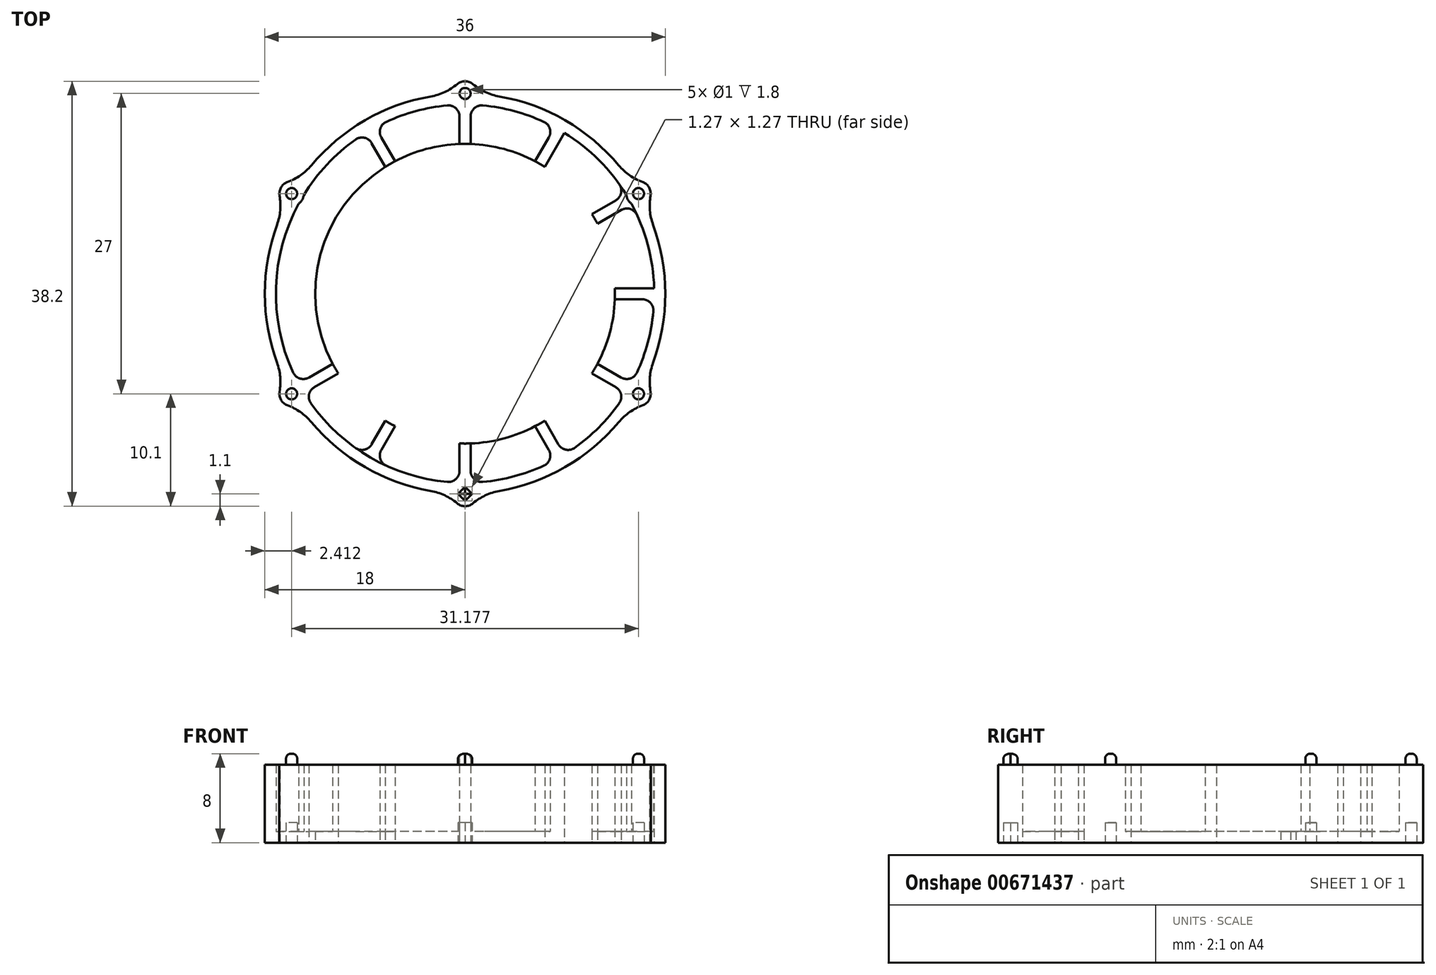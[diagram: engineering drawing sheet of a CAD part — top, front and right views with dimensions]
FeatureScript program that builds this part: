
annotation { "Feature Type Name" : "Feature", "Feature Type Description" : "" }
export const myFeature = defineFeature(function(context is Context, id is Id, definition is map)
    precondition{}
    {
        {
            var Q0;
            Q0=qCreatedBy(makeId("Top.planeOp"),FACE);
            var sketch = newSketch(context, id + "F0", { "sketchPlane" : qUnion([Q0])});
            skCircle(sketch, "E0", {"center": v(0, 0) * mm, "radius": 18 * mm});
            skCircle(sketch, "E1.0", {"center": v(0, 0) * mm, "radius": 17 * mm});
            skLineSegment(sketch, "E2.bottom", {"start": v(8.56, 15.83) * mm, "end": v(9.43, 15.33) * mm});
            skLineSegment(sketch, "E2.top", {"start": v(-9.43, -15.33) * mm, "end": v(-8.56, -15.83) * mm});
            skLineSegment(sketch, "E2.left", {"start": v(8.56, 15.83) * mm, "end": v(-9.43, -15.33) * mm});
            skLineSegment(sketch, "E2.right", {"start": v(9.43, 15.33) * mm, "end": v(-8.56, -15.83) * mm});
            skLineSegment(sketch, "E3.bottom", {"start": v(15.33, 9.43) * mm, "end": v(15.83, 8.56) * mm});
            skLineSegment(sketch, "E3.top", {"start": v(-15.83, -8.56) * mm, "end": v(-15.33, -9.43) * mm});
            skLineSegment(sketch, "E3.left", {"start": v(15.33, 9.43) * mm, "end": v(-15.83, -8.56) * mm});
            skLineSegment(sketch, "E3.right", {"start": v(15.83, 8.56) * mm, "end": v(-15.33, -9.43) * mm});
            skLineSegment(sketch, "E4", {"start": v(-38.35, 0) * mm, "end": v(39.17, 0) * mm, "construction": true});
            skLineSegment(sketch, "E5", {"start": v(0, 42.5) * mm, "end": v(0, -42.47) * mm, "construction": true});
            skLineSegment(sketch, "E6.bottom", {"start": v(-18, 0.5) * mm, "end": v(18, 0.5) * mm});
            skLineSegment(sketch, "E6.top", {"start": v(-18, -0.5) * mm, "end": v(18, -0.5) * mm});
            skLineSegment(sketch, "E6.left", {"start": v(-18, 0.5) * mm, "end": v(-18, -0.5) * mm});
            skLineSegment(sketch, "E6.right", {"start": v(18, 0.5) * mm, "end": v(18, -0.5) * mm});
            skLineSegment(sketch, "E7.bottom", {"start": v(-15.33, 9.43) * mm, "end": v(15.83, -8.56) * mm});
            skLineSegment(sketch, "E7.top", {"start": v(-15.83, 8.56) * mm, "end": v(15.33, -9.43) * mm});
            skLineSegment(sketch, "E7.left", {"start": v(-15.33, 9.43) * mm, "end": v(-15.83, 8.56) * mm});
            skLineSegment(sketch, "E7.right", {"start": v(15.83, -8.56) * mm, "end": v(15.33, -9.43) * mm});
            skLineSegment(sketch, "E8.bottom", {"start": v(-0.5, 18) * mm, "end": v(0.5, 18) * mm});
            skLineSegment(sketch, "E8.top", {"start": v(-0.5, -18) * mm, "end": v(0.5, -18) * mm});
            skLineSegment(sketch, "E8.left", {"start": v(-0.5, 18) * mm, "end": v(-0.5, -18) * mm});
            skLineSegment(sketch, "E8.right", {"start": v(0.5, 18) * mm, "end": v(0.5, -18) * mm});
            skLineSegment(sketch, "E9.bottom", {"start": v(-9.43, 15.33) * mm, "end": v(-8.56, 15.83) * mm});
            skLineSegment(sketch, "E9.top", {"start": v(8.56, -15.83) * mm, "end": v(9.43, -15.33) * mm});
            skLineSegment(sketch, "E9.left", {"start": v(-9.43, 15.33) * mm, "end": v(8.56, -15.83) * mm});
            skLineSegment(sketch, "E9.right", {"start": v(-8.56, 15.83) * mm, "end": v(9.43, -15.33) * mm});
            skCircle(sketch, "E10", {"center": v(0, 0) * mm, "radius": 13.47 * mm});
            skSolve(sketch);
        }
        {
            var Q0;
            Q0=qCreatedBy(makeId("Top.planeOp"),FACE);
            var sketch = newSketch(context, id + "F1", { "sketchPlane" : qUnion([Q0])});
            skCircle(sketch, "E11", {"center": v(0, 0) * mm, "radius": 18 * mm});
            skCircle(sketch, "E12", {"center": v(0, 0) * mm, "radius": 17 * mm});
            skSolve(sketch);
        }
        {
            var Q0;
            Q0=makeQuery(id+"F1.imprint","IMPRINT",FACE,{"disambiguationData":[TD([[makeQuery(id+"F1.imprint","IMPRINT",EDGE,{"derivedFrom":sQuery(id+"F1.wireOp",EDGE,"E11")}),1.0]])]});
            extrude(context, id + "F2", {"entities" : qUnion([Q0]), "depth" : 7 * mm, "offsetDistance" : 25 * mm});
        }
        {
            var Q0;
            {var subQ0=sQuery(id+"F0.wireOp",EDGE,"E2.right");var subQ1=sQuery(id+"F0.wireOp",EDGE,"E1.0");var subQ2=makeQuery(id+"F0.imprint","INTERSECT",VERTEX,{"disambiguationData":[OD(0.0)],"derivedFrom":[subQ1,subQ0]});Q0=makeQuery(id+"F0.imprint","IMPRINT",FACE,{"disambiguationData":[TD([[makeQuery(id+"F0.imprint","IMPRINT",EDGE,{"disambiguationData":[TD([[subQ2,-1.0]])],"derivedFrom":subQ1}),1.0]])]});}
            var Q1;
            {var subQ0=sQuery(id+"F0.wireOp",EDGE,"E6.bottom");var subQ1=sQuery(id+"F0.wireOp",EDGE,"E1.0");var subQ2=makeQuery(id+"F0.imprint","INTERSECT",VERTEX,{"disambiguationData":[OD(0.0)],"derivedFrom":[subQ1,subQ0]});Q1=makeQuery(id+"F0.imprint","IMPRINT",FACE,{"disambiguationData":[TD([[makeQuery(id+"F0.imprint","IMPRINT",EDGE,{"disambiguationData":[TD([[subQ2,1.0]])],"derivedFrom":subQ1}),1.0]])]});}
            var Q2;
            {var subQ0=sQuery(id+"F0.wireOp",EDGE,"E8.left");var subQ1=sQuery(id+"F0.wireOp",EDGE,"E1.0");var subQ2=makeQuery(id+"F0.imprint","INTERSECT",VERTEX,{"disambiguationData":[OD(1.0)],"derivedFrom":[subQ1,subQ0]});Q2=makeQuery(id+"F0.imprint","IMPRINT",FACE,{"disambiguationData":[TD([[makeQuery(id+"F0.imprint","IMPRINT",EDGE,{"disambiguationData":[TD([[subQ2,-1.0]])],"derivedFrom":subQ1}),1.0]])]});}
            var Q3;
            {var subQ0=sQuery(id+"F0.wireOp",EDGE,"E3.left");var subQ1=sQuery(id+"F0.wireOp",EDGE,"E1.0");var subQ2=makeQuery(id+"F0.imprint","INTERSECT",VERTEX,{"disambiguationData":[OD(1.0)],"derivedFrom":[subQ1,subQ0]});Q3=makeQuery(id+"F0.imprint","IMPRINT",FACE,{"disambiguationData":[TD([[makeQuery(id+"F0.imprint","IMPRINT",EDGE,{"disambiguationData":[TD([[subQ2,-1.0]])],"derivedFrom":subQ1}),1.0]])]});}
            var Q4;
            {var subQ0=sQuery(id+"F0.wireOp",EDGE,"E9.right");var subQ1=sQuery(id+"F0.wireOp",EDGE,"E1.0");var subQ2=makeQuery(id+"F0.imprint","INTERSECT",VERTEX,{"disambiguationData":[OD(0.0)],"derivedFrom":[subQ1,subQ0]});Q4=makeQuery(id+"F0.imprint","IMPRINT",FACE,{"disambiguationData":[TD([[makeQuery(id+"F0.imprint","IMPRINT",EDGE,{"disambiguationData":[TD([[subQ2,-1.0]])],"derivedFrom":subQ1}),1.0]])]});}
            var Q5;
            {var subQ0=sQuery(id+"F0.wireOp",EDGE,"E8.right");var subQ1=sQuery(id+"F0.wireOp",EDGE,"E1.0");var subQ2=makeQuery(id+"F0.imprint","INTERSECT",VERTEX,{"disambiguationData":[OD(0.0)],"derivedFrom":[subQ1,subQ0]});Q5=makeQuery(id+"F0.imprint","IMPRINT",FACE,{"disambiguationData":[TD([[makeQuery(id+"F0.imprint","IMPRINT",EDGE,{"disambiguationData":[TD([[subQ2,-1.0]])],"derivedFrom":subQ1}),1.0]])]});}
            var Q6;
            {var subQ0=sQuery(id+"F0.wireOp",EDGE,"E7.top");var subQ1=sQuery(id+"F0.wireOp",EDGE,"E1.0");var subQ2=makeQuery(id+"F0.imprint","INTERSECT",VERTEX,{"disambiguationData":[OD(1.0)],"derivedFrom":[subQ1,subQ0]});Q6=makeQuery(id+"F0.imprint","IMPRINT",FACE,{"disambiguationData":[TD([[makeQuery(id+"F0.imprint","IMPRINT",EDGE,{"disambiguationData":[TD([[subQ2,-1.0]])],"derivedFrom":subQ1}),1.0]])]});}
            var Q7;
            {var subQ0=sQuery(id+"F0.wireOp",EDGE,"E9.left");var subQ1=sQuery(id+"F0.wireOp",EDGE,"E1.0");var subQ2=makeQuery(id+"F0.imprint","INTERSECT",VERTEX,{"disambiguationData":[OD(1.0)],"derivedFrom":[subQ1,subQ0]});Q7=makeQuery(id+"F0.imprint","IMPRINT",FACE,{"disambiguationData":[TD([[makeQuery(id+"F0.imprint","IMPRINT",EDGE,{"disambiguationData":[TD([[subQ2,-1.0]])],"derivedFrom":subQ1}),1.0]])]});}
            extrude(context, id + "F3", {"entities" : qUnion([Q0, Q1, Q2, Q3, Q4, Q5, Q6, Q7]), "operationType" : NewBodyOperationType.ADD, "depth" : 7 * mm, "offsetDistance" : 25 * mm});
        }
        {
            var Q0;
            Q0=makeQuery(id+"F1.imprint","IMPRINT",FACE,{"disambiguationData":[TD([[makeQuery(id+"F1.imprint","IMPRINT",EDGE,{"derivedFrom":sQuery(id+"F1.wireOp",EDGE,"E11")}),1.0]])]});
            var Q1;
            Q1=makeQuery(id+"F1.imprint","IMPRINT",FACE,{"disambiguationData":[TD([[makeQuery(id+"F1.imprint","IMPRINT",EDGE,{"derivedFrom":sQuery(id+"F1.wireOp",EDGE,"E12")}),1.0]])]});
            extrude(context, id + "F4", {"entities" : qUnion([Q0, Q1]), "operationType" : NewBodyOperationType.ADD, "depth" : 1 * mm, "offsetDistance" : 25 * mm});
        }
        {
            var Q0;
            Q0=qCreatedBy(makeId("Top.planeOp"),FACE);
            var sketch = newSketch(context, id + "F5", { "sketchPlane" : qUnion([Q0])});
            skCircle(sketch, "E13", {"center": v(0, 0) * mm, "radius": 18 * mm});
            skLineSegment(sketch, "E14", {"start": v(0, 18) * mm, "end": v(0, -18) * mm, "construction": true});
            skLineSegment(sketch, "E15", {"start": v(15.59, 9) * mm, "end": v(0, 0) * mm, "construction": true});
            skLineSegment(sketch, "E16", {"start": v(9, 15.59) * mm, "end": v(0, 0) * mm, "construction": true});
            skLineSegment(sketch, "E17", {"start": v(0, 0) * mm, "end": v(18, 0) * mm, "construction": true});
            skLineSegment(sketch, "E18", {"start": v(0, 0) * mm, "end": v(15.59, -9) * mm, "construction": true});
            skLineSegment(sketch, "E19", {"start": v(0, 0) * mm, "end": v(9, -15.59) * mm, "construction": true});
            skLineSegment(sketch, "E20", {"start": v(0, 0) * mm, "end": v(-9, 15.59) * mm, "construction": true});
            skLineSegment(sketch, "E21", {"start": v(0, 0) * mm, "end": v(-15.59, 9) * mm, "construction": true});
            skLineSegment(sketch, "E22", {"start": v(0, 0) * mm, "end": v(-18, 0) * mm, "construction": true});
            skLineSegment(sketch, "E23", {"start": v(0, 0) * mm, "end": v(-15.59, -9) * mm, "construction": true});
            skLineSegment(sketch, "E24", {"start": v(0, 0) * mm, "end": v(-9, -15.59) * mm, "construction": true});
            skCircle(sketch, "E25", {"center": v(0, 18) * mm, "radius": 1.1 * mm});
            skCircle(sketch, "E26", {"center": v(15.59, 9) * mm, "radius": 1.1 * mm});
            skCircle(sketch, "E27", {"center": v(15.59, -9) * mm, "radius": 1.1 * mm});
            skCircle(sketch, "E28", {"center": v(0, -18) * mm, "radius": 1.1 * mm});
            skCircle(sketch, "E29", {"center": v(-15.59, -9) * mm, "radius": 1.1 * mm});
            skCircle(sketch, "E30", {"center": v(-15.59, 9) * mm, "radius": 1.1 * mm});
            skCircle(sketch, "E31", {"center": v(-15.59, 9) * mm, "radius": 0.5 * mm});
            skCircle(sketch, "E32", {"center": v(0, 18) * mm, "radius": 0.5 * mm});
            skCircle(sketch, "E33", {"center": v(15.59, 9) * mm, "radius": 0.5 * mm});
            skCircle(sketch, "E34", {"center": v(15.59, -9) * mm, "radius": 0.5 * mm});
            skCircle(sketch, "E35", {"center": v(-15.59, -9) * mm, "radius": 0.5 * mm});
            skLineSegment(sketch, "E36.bottom", {"start": v(0.64, -18) * mm, "end": v(0, -18.64) * mm});
            skLineSegment(sketch, "E36.top", {"start": v(0, -17.36) * mm, "end": v(-0.64, -18) * mm});
            skLineSegment(sketch, "E36.left", {"start": v(0.64, -18) * mm, "end": v(0, -17.36) * mm});
            skLineSegment(sketch, "E36.right", {"start": v(0, -18.64) * mm, "end": v(-0.64, -18) * mm});
            skSolve(sketch);
        }
        {
            var Q0;
            {var subQ0=sQuery(id+"F5.wireOp",EDGE,"E30");var subQ1=sQuery(id+"F5.wireOp",EDGE,"E13");var subQ2=makeQuery(id+"F5.imprint","INTERSECT",VERTEX,{"disambiguationData":[OD(0.0)],"derivedFrom":[subQ1,subQ0]});Q0=makeQuery(id+"F5.imprint","IMPRINT",FACE,{"disambiguationData":[TD([[makeQuery(id+"F5.imprint","IMPRINT",EDGE,{"disambiguationData":[TD([[subQ2,-1.0]])],"derivedFrom":subQ1}),1.0]])]});}
            var Q1;
            {var subQ0=sQuery(id+"F5.wireOp",EDGE,"E30");var subQ1=sQuery(id+"F5.wireOp",EDGE,"E13");var subQ2=makeQuery(id+"F5.imprint","INTERSECT",VERTEX,{"disambiguationData":[OD(0.0)],"derivedFrom":[subQ1,subQ0]});Q1=makeQuery(id+"F5.imprint","IMPRINT",FACE,{"disambiguationData":[TD([[makeQuery(id+"F5.imprint","IMPRINT",EDGE,{"disambiguationData":[TD([[subQ2,-1.0]])],"derivedFrom":subQ1}),-1.0]])]});}
            var Q2;
            {var subQ0=sQuery(id+"F5.wireOp",EDGE,"E25");var subQ1=sQuery(id+"F5.wireOp",EDGE,"E13");var subQ2=makeQuery(id+"F5.imprint","INTERSECT",VERTEX,{"disambiguationData":[OD(0.0)],"derivedFrom":[subQ1,subQ0]});Q2=makeQuery(id+"F5.imprint","IMPRINT",FACE,{"disambiguationData":[TD([[makeQuery(id+"F5.imprint","IMPRINT",EDGE,{"disambiguationData":[TD([[subQ2,-1.0]])],"derivedFrom":subQ1}),1.0]])]});}
            var Q3;
            {var subQ0=sQuery(id+"F5.wireOp",EDGE,"E25");var subQ1=sQuery(id+"F5.wireOp",EDGE,"E13");var subQ2=makeQuery(id+"F5.imprint","INTERSECT",VERTEX,{"disambiguationData":[OD(0.0)],"derivedFrom":[subQ1,subQ0]});Q3=makeQuery(id+"F5.imprint","IMPRINT",FACE,{"disambiguationData":[TD([[makeQuery(id+"F5.imprint","IMPRINT",EDGE,{"disambiguationData":[TD([[subQ2,-1.0]])],"derivedFrom":subQ1}),-1.0]])]});}
            var Q4;
            {var subQ0=sQuery(id+"F5.wireOp",EDGE,"E26");var subQ1=sQuery(id+"F5.wireOp",EDGE,"E13");var subQ2=makeQuery(id+"F5.imprint","INTERSECT",VERTEX,{"disambiguationData":[OD(0.0)],"derivedFrom":[subQ1,subQ0]});Q4=makeQuery(id+"F5.imprint","IMPRINT",FACE,{"disambiguationData":[TD([[makeQuery(id+"F5.imprint","IMPRINT",EDGE,{"disambiguationData":[TD([[subQ2,-1.0]])],"derivedFrom":subQ1}),-1.0]])]});}
            var Q5;
            {var subQ0=sQuery(id+"F5.wireOp",EDGE,"E26");var subQ1=sQuery(id+"F5.wireOp",EDGE,"E13");var subQ2=makeQuery(id+"F5.imprint","INTERSECT",VERTEX,{"disambiguationData":[OD(0.0)],"derivedFrom":[subQ1,subQ0]});Q5=makeQuery(id+"F5.imprint","IMPRINT",FACE,{"disambiguationData":[TD([[makeQuery(id+"F5.imprint","IMPRINT",EDGE,{"disambiguationData":[TD([[subQ2,-1.0]])],"derivedFrom":subQ1}),1.0]])]});}
            var Q6;
            {var subQ0=sQuery(id+"F5.wireOp",EDGE,"E29");var subQ1=sQuery(id+"F5.wireOp",EDGE,"E13");var subQ2=makeQuery(id+"F5.imprint","INTERSECT",VERTEX,{"disambiguationData":[OD(0.0)],"derivedFrom":[subQ1,subQ0]});Q6=makeQuery(id+"F5.imprint","IMPRINT",FACE,{"disambiguationData":[TD([[makeQuery(id+"F5.imprint","IMPRINT",EDGE,{"disambiguationData":[TD([[subQ2,-1.0]])],"derivedFrom":subQ1}),1.0]])]});}
            var Q7;
            {var subQ0=sQuery(id+"F5.wireOp",EDGE,"E29");var subQ1=sQuery(id+"F5.wireOp",EDGE,"E13");var subQ2=makeQuery(id+"F5.imprint","INTERSECT",VERTEX,{"disambiguationData":[OD(0.0)],"derivedFrom":[subQ1,subQ0]});Q7=makeQuery(id+"F5.imprint","IMPRINT",FACE,{"disambiguationData":[TD([[makeQuery(id+"F5.imprint","IMPRINT",EDGE,{"disambiguationData":[TD([[subQ2,-1.0]])],"derivedFrom":subQ1}),-1.0]])]});}
            var Q8;
            {var subQ3=sQuery(id+"F5.wireOp",EDGE,"E13");var subQ5=sQuery(id+"F5.wireOp",EDGE,"E28");var subQ6=makeQuery(id+"F5.imprint","INTERSECT",VERTEX,{"disambiguationData":[OD(0.0)],"derivedFrom":[subQ3,subQ5]});Q8=makeQuery(id+"F5.imprint","IMPRINT",FACE,{"disambiguationData":[TD([[makeQuery(id+"F5.imprint","IMPRINT",EDGE,{"disambiguationData":[TD([[subQ6,-1.0]])],"derivedFrom":subQ3}),1.0]])]});}
            var Q9;
            {var subQ6=sQuery(id+"F5.wireOp",EDGE,"E36.bottom");Q9=makeQuery(id+"F5.imprint","IMPRINT",FACE,{"disambiguationData":[TD([[makeQuery(id+"F5.imprint","IMPRINT",EDGE,{"derivedFrom":subQ6}),1.0]])]});}
            var Q10;
            {var subQ0=sQuery(id+"F5.wireOp",EDGE,"E27");var subQ1=sQuery(id+"F5.wireOp",EDGE,"E13");var subQ2=makeQuery(id+"F5.imprint","INTERSECT",VERTEX,{"disambiguationData":[OD(0.0)],"derivedFrom":[subQ1,subQ0]});Q10=makeQuery(id+"F5.imprint","IMPRINT",FACE,{"disambiguationData":[TD([[makeQuery(id+"F5.imprint","IMPRINT",EDGE,{"disambiguationData":[TD([[subQ2,-1.0]])],"derivedFrom":subQ1}),-1.0]])]});}
            var Q11;
            {var subQ0=sQuery(id+"F5.wireOp",EDGE,"E27");var subQ1=sQuery(id+"F5.wireOp",EDGE,"E13");var subQ2=makeQuery(id+"F5.imprint","INTERSECT",VERTEX,{"disambiguationData":[OD(0.0)],"derivedFrom":[subQ1,subQ0]});Q11=makeQuery(id+"F5.imprint","IMPRINT",FACE,{"disambiguationData":[TD([[makeQuery(id+"F5.imprint","IMPRINT",EDGE,{"disambiguationData":[TD([[subQ2,-1.0]])],"derivedFrom":subQ1}),1.0]])]});}
            var Q12;
            {var subQ0=sQuery(id+"F5.wireOp",EDGE,"E31");var subQ1=sQuery(id+"F5.wireOp",EDGE,"E13");var subQ2=makeQuery(id+"F5.imprint","INTERSECT",VERTEX,{"disambiguationData":[OD(0.0)],"derivedFrom":[subQ1,subQ0]});Q12=makeQuery(id+"F5.imprint","IMPRINT",FACE,{"disambiguationData":[TD([[makeQuery(id+"F5.imprint","IMPRINT",EDGE,{"disambiguationData":[TD([[subQ2,-1.0]])],"derivedFrom":subQ1}),1.0]])]});}
            var Q13;
            {var subQ0=sQuery(id+"F5.wireOp",EDGE,"E31");var subQ1=sQuery(id+"F5.wireOp",EDGE,"E13");var subQ2=makeQuery(id+"F5.imprint","INTERSECT",VERTEX,{"disambiguationData":[OD(0.0)],"derivedFrom":[subQ1,subQ0]});Q13=makeQuery(id+"F5.imprint","IMPRINT",FACE,{"disambiguationData":[TD([[makeQuery(id+"F5.imprint","IMPRINT",EDGE,{"disambiguationData":[TD([[subQ2,-1.0]])],"derivedFrom":subQ1}),-1.0]])]});}
            var Q14;
            {var subQ0=sQuery(id+"F5.wireOp",EDGE,"E32");var subQ1=sQuery(id+"F5.wireOp",EDGE,"E13");var subQ2=makeQuery(id+"F5.imprint","INTERSECT",VERTEX,{"disambiguationData":[OD(0.0)],"derivedFrom":[subQ1,subQ0]});Q14=makeQuery(id+"F5.imprint","IMPRINT",FACE,{"disambiguationData":[TD([[makeQuery(id+"F5.imprint","IMPRINT",EDGE,{"disambiguationData":[TD([[subQ2,-1.0]])],"derivedFrom":subQ1}),-1.0]])]});}
            var Q15;
            {var subQ0=sQuery(id+"F5.wireOp",EDGE,"E32");var subQ1=sQuery(id+"F5.wireOp",EDGE,"E13");var subQ2=makeQuery(id+"F5.imprint","INTERSECT",VERTEX,{"disambiguationData":[OD(0.0)],"derivedFrom":[subQ1,subQ0]});Q15=makeQuery(id+"F5.imprint","IMPRINT",FACE,{"disambiguationData":[TD([[makeQuery(id+"F5.imprint","IMPRINT",EDGE,{"disambiguationData":[TD([[subQ2,-1.0]])],"derivedFrom":subQ1}),1.0]])]});}
            var Q16;
            {var subQ0=sQuery(id+"F5.wireOp",EDGE,"E33");var subQ1=sQuery(id+"F5.wireOp",EDGE,"E13");var subQ2=makeQuery(id+"F5.imprint","INTERSECT",VERTEX,{"disambiguationData":[OD(0.0)],"derivedFrom":[subQ1,subQ0]});Q16=makeQuery(id+"F5.imprint","IMPRINT",FACE,{"disambiguationData":[TD([[makeQuery(id+"F5.imprint","IMPRINT",EDGE,{"disambiguationData":[TD([[subQ2,-1.0]])],"derivedFrom":subQ1}),-1.0]])]});}
            var Q17;
            {var subQ0=sQuery(id+"F5.wireOp",EDGE,"E33");var subQ1=sQuery(id+"F5.wireOp",EDGE,"E13");var subQ2=makeQuery(id+"F5.imprint","INTERSECT",VERTEX,{"disambiguationData":[OD(0.0)],"derivedFrom":[subQ1,subQ0]});Q17=makeQuery(id+"F5.imprint","IMPRINT",FACE,{"disambiguationData":[TD([[makeQuery(id+"F5.imprint","IMPRINT",EDGE,{"disambiguationData":[TD([[subQ2,-1.0]])],"derivedFrom":subQ1}),1.0]])]});}
            var Q18;
            {var subQ0=sQuery(id+"F5.wireOp",EDGE,"E34");var subQ1=sQuery(id+"F5.wireOp",EDGE,"E13");var subQ2=makeQuery(id+"F5.imprint","INTERSECT",VERTEX,{"disambiguationData":[OD(0.0)],"derivedFrom":[subQ1,subQ0]});Q18=makeQuery(id+"F5.imprint","IMPRINT",FACE,{"disambiguationData":[TD([[makeQuery(id+"F5.imprint","IMPRINT",EDGE,{"disambiguationData":[TD([[subQ2,-1.0]])],"derivedFrom":subQ1}),-1.0]])]});}
            var Q19;
            {var subQ0=sQuery(id+"F5.wireOp",EDGE,"E34");var subQ1=sQuery(id+"F5.wireOp",EDGE,"E13");var subQ2=makeQuery(id+"F5.imprint","INTERSECT",VERTEX,{"disambiguationData":[OD(0.0)],"derivedFrom":[subQ1,subQ0]});Q19=makeQuery(id+"F5.imprint","IMPRINT",FACE,{"disambiguationData":[TD([[makeQuery(id+"F5.imprint","IMPRINT",EDGE,{"disambiguationData":[TD([[subQ2,-1.0]])],"derivedFrom":subQ1}),1.0]])]});}
            var Q20;
            {var subQ1=sQuery(id+"F5.wireOp",EDGE,"E36.bottom");Q20=makeQuery(id+"F5.imprint","IMPRINT",FACE,{"disambiguationData":[TD([[makeQuery(id+"F5.imprint","IMPRINT",EDGE,{"derivedFrom":subQ1}),-1.0]])]});}
            var Q21;
            {var subQ0=sQuery(id+"F5.wireOp",EDGE,"E35");var subQ1=sQuery(id+"F5.wireOp",EDGE,"E13");var subQ2=makeQuery(id+"F5.imprint","INTERSECT",VERTEX,{"disambiguationData":[OD(0.0)],"derivedFrom":[subQ1,subQ0]});Q21=makeQuery(id+"F5.imprint","IMPRINT",FACE,{"disambiguationData":[TD([[makeQuery(id+"F5.imprint","IMPRINT",EDGE,{"disambiguationData":[TD([[subQ2,-1.0]])],"derivedFrom":subQ1}),-1.0]])]});}
            var Q22;
            {var subQ0=sQuery(id+"F5.wireOp",EDGE,"E35");var subQ1=sQuery(id+"F5.wireOp",EDGE,"E13");var subQ2=makeQuery(id+"F5.imprint","INTERSECT",VERTEX,{"disambiguationData":[OD(0.0)],"derivedFrom":[subQ1,subQ0]});Q22=makeQuery(id+"F5.imprint","IMPRINT",FACE,{"disambiguationData":[TD([[makeQuery(id+"F5.imprint","IMPRINT",EDGE,{"disambiguationData":[TD([[subQ2,-1.0]])],"derivedFrom":subQ1}),1.0]])]});}
            var Q23;
            {var subQ0=sQuery(id+"F5.wireOp",EDGE,"E36.top");var subQ1=sQuery(id+"F5.wireOp",EDGE,"E13");var subQ2=makeQuery(id+"F5.imprint","INTERSECT",VERTEX,{"derivedFrom":[subQ1,subQ0]});Q23=makeQuery(id+"F5.imprint","IMPRINT",FACE,{"disambiguationData":[TD([[makeQuery(id+"F5.imprint","IMPRINT",EDGE,{"disambiguationData":[TD([[subQ2,-1.0]])],"derivedFrom":subQ1}),1.0]])]});}
            extrude(context, id + "F6", {"entities" : qUnion([Q0, Q1, Q2, Q3, Q4, Q5, Q6, Q7, Q8, Q9, Q10, Q11, Q12, Q13, Q14, Q15, Q16, Q17, Q18, Q19, Q20, Q21, Q22, Q23]), "operationType" : NewBodyOperationType.ADD, "depth" : 7 * mm, "offsetDistance" : 25 * mm});
        }
        {
            var Q0;
            {var subQ0=sQuery(id+"F0.wireOp",EDGE,"E8.right");var subQ1=sQuery(id+"F0.wireOp",EDGE,"E1.0");Q0=makeQuery(id+"F3.opExtrude","SWEPT_EDGE",EDGE,{"disambiguationData":[OSD([subQ1,subQ0]),TDD([makeQuery(id+"F0.imprint","INTERSECT",VERTEX,{"disambiguationData":[OD(1.0)],"derivedFrom":[subQ1,subQ0]})])]});}
            var Q1;
            {var subQ0=sQuery(id+"F0.wireOp",EDGE,"E2.left");var subQ1=sQuery(id+"F0.wireOp",EDGE,"E1.0");Q1=makeQuery(id+"F3.opExtrude","SWEPT_EDGE",EDGE,{"disambiguationData":[OSD([subQ1,subQ0]),TDD([makeQuery(id+"F0.imprint","INTERSECT",VERTEX,{"disambiguationData":[OD(1.0)],"derivedFrom":[subQ1,subQ0]})])]});}
            var Q2;
            {var subQ0=sQuery(id+"F0.wireOp",EDGE,"E3.left");var subQ1=sQuery(id+"F0.wireOp",EDGE,"E1.0");Q2=makeQuery(id+"F3.opExtrude","SWEPT_EDGE",EDGE,{"disambiguationData":[OSD([subQ1,subQ0]),TDD([makeQuery(id+"F0.imprint","INTERSECT",VERTEX,{"disambiguationData":[OD(1.0)],"derivedFrom":[subQ1,subQ0]})])]});}
            var Q3;
            {var subQ0=sQuery(id+"F0.wireOp",EDGE,"E6.bottom");var subQ1=sQuery(id+"F0.wireOp",EDGE,"E1.0");Q3=makeQuery(id+"F3.opExtrude","SWEPT_EDGE",EDGE,{"disambiguationData":[OSD([subQ1,subQ0]),TDD([makeQuery(id+"F0.imprint","INTERSECT",VERTEX,{"disambiguationData":[OD(1.0)],"derivedFrom":[subQ1,subQ0]})])]});}
            var Q4;
            {var subQ0=sQuery(id+"F0.wireOp",EDGE,"E9.right");var subQ1=sQuery(id+"F0.wireOp",EDGE,"E1.0");Q4=makeQuery(id+"F3.opExtrude","SWEPT_EDGE",EDGE,{"disambiguationData":[OSD([subQ1,subQ0]),TDD([makeQuery(id+"F0.imprint","INTERSECT",VERTEX,{"disambiguationData":[OD(1.0)],"derivedFrom":[subQ1,subQ0]})])]});}
            var Q5;
            {var subQ0=sQuery(id+"F0.wireOp",EDGE,"E7.bottom");var subQ1=sQuery(id+"F0.wireOp",EDGE,"E1.0");Q5=makeQuery(id+"F3.opExtrude","SWEPT_EDGE",EDGE,{"disambiguationData":[OSD([subQ1,subQ0]),TDD([makeQuery(id+"F0.imprint","INTERSECT",VERTEX,{"disambiguationData":[OD(1.0)],"derivedFrom":[subQ1,subQ0]})])]});}
            var Q6;
            {var subQ0=sQuery(id+"F0.wireOp",EDGE,"E8.left");var subQ1=sQuery(id+"F0.wireOp",EDGE,"E1.0");Q6=makeQuery(id+"F3.opExtrude","SWEPT_EDGE",EDGE,{"disambiguationData":[OSD([subQ1,subQ0]),TDD([makeQuery(id+"F0.imprint","INTERSECT",VERTEX,{"disambiguationData":[OD(0.0)],"derivedFrom":[subQ1,subQ0]})])]});}
            var Q7;
            {var subQ0=sQuery(id+"F0.wireOp",EDGE,"E2.left");var subQ1=sQuery(id+"F0.wireOp",EDGE,"E1.0");Q7=makeQuery(id+"F3.opExtrude","SWEPT_EDGE",EDGE,{"disambiguationData":[OSD([subQ1,subQ0]),TDD([makeQuery(id+"F0.imprint","INTERSECT",VERTEX,{"disambiguationData":[OD(0.0)],"derivedFrom":[subQ1,subQ0]})])]});}
            var Q8;
            {var subQ0=sQuery(id+"F0.wireOp",EDGE,"E3.left");var subQ1=sQuery(id+"F0.wireOp",EDGE,"E1.0");Q8=makeQuery(id+"F3.opExtrude","SWEPT_EDGE",EDGE,{"disambiguationData":[OSD([subQ1,subQ0]),TDD([makeQuery(id+"F0.imprint","INTERSECT",VERTEX,{"disambiguationData":[OD(0.0)],"derivedFrom":[subQ1,subQ0]})])]});}
            var Q9;
            {var subQ0=sQuery(id+"F0.wireOp",EDGE,"E6.top");var subQ1=sQuery(id+"F0.wireOp",EDGE,"E1.0");Q9=makeQuery(id+"F3.opExtrude","SWEPT_EDGE",EDGE,{"disambiguationData":[OSD([subQ1,subQ0]),TDD([makeQuery(id+"F0.imprint","INTERSECT",VERTEX,{"disambiguationData":[OD(1.0)],"derivedFrom":[subQ1,subQ0]})])]});}
            var Q10;
            {var subQ0=sQuery(id+"F0.wireOp",EDGE,"E7.top");var subQ1=sQuery(id+"F0.wireOp",EDGE,"E1.0");Q10=makeQuery(id+"F3.opExtrude","SWEPT_EDGE",EDGE,{"disambiguationData":[OSD([subQ1,subQ0]),TDD([makeQuery(id+"F0.imprint","INTERSECT",VERTEX,{"disambiguationData":[OD(0.0)],"derivedFrom":[subQ1,subQ0]})])]});}
            var Q11;
            {var subQ0=sQuery(id+"F0.wireOp",EDGE,"E6.top");var subQ1=sQuery(id+"F0.wireOp",EDGE,"E1.0");Q11=makeQuery(id+"F3.opExtrude","SWEPT_EDGE",EDGE,{"disambiguationData":[OSD([subQ1,subQ0]),TDD([makeQuery(id+"F0.imprint","INTERSECT",VERTEX,{"disambiguationData":[OD(0.0)],"derivedFrom":[subQ1,subQ0]})])]});}
            var Q12;
            {var subQ0=sQuery(id+"F0.wireOp",EDGE,"E9.left");var subQ1=sQuery(id+"F0.wireOp",EDGE,"E1.0");Q12=makeQuery(id+"F3.opExtrude","SWEPT_EDGE",EDGE,{"disambiguationData":[OSD([subQ1,subQ0]),TDD([makeQuery(id+"F0.imprint","INTERSECT",VERTEX,{"disambiguationData":[OD(0.0)],"derivedFrom":[subQ1,subQ0]})])]});}
            var Q13;
            {var subQ0=sQuery(id+"F0.wireOp",EDGE,"E8.right");var subQ1=sQuery(id+"F0.wireOp",EDGE,"E1.0");Q13=makeQuery(id+"F3.opExtrude","SWEPT_EDGE",EDGE,{"disambiguationData":[OSD([subQ1,subQ0]),TDD([makeQuery(id+"F0.imprint","INTERSECT",VERTEX,{"disambiguationData":[OD(0.0)],"derivedFrom":[subQ1,subQ0]})])]});}
            var Q14;
            {var subQ0=sQuery(id+"F0.wireOp",EDGE,"E7.bottom");var subQ1=sQuery(id+"F0.wireOp",EDGE,"E1.0");Q14=makeQuery(id+"F3.opExtrude","SWEPT_EDGE",EDGE,{"disambiguationData":[OSD([subQ1,subQ0]),TDD([makeQuery(id+"F0.imprint","INTERSECT",VERTEX,{"disambiguationData":[OD(0.0)],"derivedFrom":[subQ1,subQ0]})])]});}
            var Q15;
            {var subQ0=sQuery(id+"F0.wireOp",EDGE,"E9.right");var subQ1=sQuery(id+"F0.wireOp",EDGE,"E1.0");Q15=makeQuery(id+"F3.opExtrude","SWEPT_EDGE",EDGE,{"disambiguationData":[OSD([subQ1,subQ0]),TDD([makeQuery(id+"F0.imprint","INTERSECT",VERTEX,{"disambiguationData":[OD(0.0)],"derivedFrom":[subQ1,subQ0]})])]});}
            var Q16;
            {var subQ0=sQuery(id+"F0.wireOp",EDGE,"E3.right");var subQ1=sQuery(id+"F0.wireOp",EDGE,"E1.0");Q16=makeQuery(id+"F3.opExtrude","SWEPT_EDGE",EDGE,{"disambiguationData":[OSD([subQ1,subQ0]),TDD([makeQuery(id+"F0.imprint","INTERSECT",VERTEX,{"disambiguationData":[OD(1.0)],"derivedFrom":[subQ1,subQ0]})])]});}
            var Q17;
            {var subQ0=sQuery(id+"F0.wireOp",EDGE,"E2.right");var subQ1=sQuery(id+"F0.wireOp",EDGE,"E1.0");Q17=makeQuery(id+"F3.opExtrude","SWEPT_EDGE",EDGE,{"disambiguationData":[OSD([subQ1,subQ0]),TDD([makeQuery(id+"F0.imprint","INTERSECT",VERTEX,{"disambiguationData":[OD(1.0)],"derivedFrom":[subQ1,subQ0]})])]});}
            var Q18;
            {var subQ0=sQuery(id+"F0.wireOp",EDGE,"E3.right");var subQ1=sQuery(id+"F0.wireOp",EDGE,"E1.0");Q18=makeQuery(id+"F3.opExtrude","SWEPT_EDGE",EDGE,{"disambiguationData":[OSD([subQ1,subQ0]),TDD([makeQuery(id+"F0.imprint","INTERSECT",VERTEX,{"disambiguationData":[OD(0.0)],"derivedFrom":[subQ1,subQ0]})])]});}
            var Q19;
            {var subQ0=sQuery(id+"F0.wireOp",EDGE,"E2.right");var subQ1=sQuery(id+"F0.wireOp",EDGE,"E1.0");Q19=makeQuery(id+"F3.opExtrude","SWEPT_EDGE",EDGE,{"disambiguationData":[OSD([subQ1,subQ0]),TDD([makeQuery(id+"F0.imprint","INTERSECT",VERTEX,{"disambiguationData":[OD(0.0)],"derivedFrom":[subQ1,subQ0]})])]});}
            var Q20;
            {var subQ0=sQuery(id+"F0.wireOp",EDGE,"E8.left");var subQ1=sQuery(id+"F0.wireOp",EDGE,"E1.0");Q20=makeQuery(id+"F3.opExtrude","SWEPT_EDGE",EDGE,{"disambiguationData":[OSD([subQ1,subQ0]),TDD([makeQuery(id+"F0.imprint","INTERSECT",VERTEX,{"disambiguationData":[OD(1.0)],"derivedFrom":[subQ1,subQ0]})])]});}
            var Q21;
            {var subQ0=sQuery(id+"F0.wireOp",EDGE,"E9.left");var subQ1=sQuery(id+"F0.wireOp",EDGE,"E1.0");Q21=makeQuery(id+"F3.opExtrude","SWEPT_EDGE",EDGE,{"disambiguationData":[OSD([subQ1,subQ0]),TDD([makeQuery(id+"F0.imprint","INTERSECT",VERTEX,{"disambiguationData":[OD(1.0)],"derivedFrom":[subQ1,subQ0]})])]});}
            var Q22;
            {var subQ0=sQuery(id+"F0.wireOp",EDGE,"E7.top");var subQ1=sQuery(id+"F0.wireOp",EDGE,"E1.0");Q22=makeQuery(id+"F3.opExtrude","SWEPT_EDGE",EDGE,{"disambiguationData":[OSD([subQ1,subQ0]),TDD([makeQuery(id+"F0.imprint","INTERSECT",VERTEX,{"disambiguationData":[OD(1.0)],"derivedFrom":[subQ1,subQ0]})])]});}
            var Q23;
            {var subQ0=sQuery(id+"F0.wireOp",EDGE,"E6.bottom");var subQ1=sQuery(id+"F0.wireOp",EDGE,"E1.0");Q23=makeQuery(id+"F3.opExtrude","SWEPT_EDGE",EDGE,{"disambiguationData":[OSD([subQ1,subQ0]),TDD([makeQuery(id+"F0.imprint","INTERSECT",VERTEX,{"disambiguationData":[OD(0.0)],"derivedFrom":[subQ1,subQ0]})])]});}
            fillet(context, id + "F7", {"entities" : qUnion([Q0, Q1, Q2, Q3, Q4, Q5, Q6, Q7, Q8, Q9, Q10, Q11, Q12, Q13, Q14, Q15, Q16, Q17, Q18, Q19, Q20, Q21, Q22, Q23]), "radius" : 1 * mm, "tangentPropagation" : true, "allowEdgeOverflow" : false});
        }
        {
            var Q0;
            Q0=makeQuery(id+"F6.boolean.opBoolean","INTERSECT",EDGE,{"disambiguationData":[OD(0.0)],"derivedFrom":[makeQuery(id+"F2.opExtrude","SWEPT_FACE",FACE,{"disambiguationData":[OSD([sQuery(id+"F1.wireOp",EDGE,"E11")])]}),makeQuery(id+"F6.opExtrude","SWEPT_FACE",FACE,{"disambiguationData":[OSD([sQuery(id+"F5.wireOp",EDGE,"E30")])]})]});
            var Q1;
            Q1=makeQuery(id+"F6.boolean.opBoolean","INTERSECT",EDGE,{"disambiguationData":[OD(1.0)],"derivedFrom":[makeQuery(id+"F2.opExtrude","SWEPT_FACE",FACE,{"disambiguationData":[OSD([sQuery(id+"F1.wireOp",EDGE,"E11")])]}),makeQuery(id+"F6.opExtrude","SWEPT_FACE",FACE,{"disambiguationData":[OSD([sQuery(id+"F5.wireOp",EDGE,"E30")])]})]});
            var Q2;
            Q2=makeQuery(id+"F6.boolean.opBoolean","INTERSECT",EDGE,{"disambiguationData":[OD(1.0)],"derivedFrom":[makeQuery(id+"F2.opExtrude","SWEPT_FACE",FACE,{"disambiguationData":[OSD([sQuery(id+"F1.wireOp",EDGE,"E11")])]}),makeQuery(id+"F6.opExtrude","SWEPT_FACE",FACE,{"disambiguationData":[OSD([sQuery(id+"F5.wireOp",EDGE,"E25")])]})]});
            var Q3;
            Q3=makeQuery(id+"F6.boolean.opBoolean","INTERSECT",EDGE,{"disambiguationData":[OD(1.0)],"derivedFrom":[makeQuery(id+"F2.opExtrude","SWEPT_FACE",FACE,{"disambiguationData":[OSD([sQuery(id+"F1.wireOp",EDGE,"E11")])]}),makeQuery(id+"F6.opExtrude","SWEPT_FACE",FACE,{"disambiguationData":[OSD([sQuery(id+"F5.wireOp",EDGE,"E29")])]})]});
            var Q4;
            Q4=makeQuery(id+"F6.boolean.opBoolean","INTERSECT",EDGE,{"disambiguationData":[OD(0.0)],"derivedFrom":[makeQuery(id+"F2.opExtrude","SWEPT_FACE",FACE,{"disambiguationData":[OSD([sQuery(id+"F1.wireOp",EDGE,"E11")])]}),makeQuery(id+"F6.opExtrude","SWEPT_FACE",FACE,{"disambiguationData":[OSD([sQuery(id+"F5.wireOp",EDGE,"E29")])]})]});
            var Q5;
            Q5=makeQuery(id+"F6.boolean.opBoolean","INTERSECT",EDGE,{"disambiguationData":[OD(1.0)],"derivedFrom":[makeQuery(id+"F2.opExtrude","SWEPT_FACE",FACE,{"disambiguationData":[OSD([sQuery(id+"F1.wireOp",EDGE,"E11")])]}),makeQuery(id+"F6.opExtrude","SWEPT_FACE",FACE,{"disambiguationData":[OSD([sQuery(id+"F5.wireOp",EDGE,"E28")])]})]});
            var Q6;
            Q6=makeQuery(id+"F6.boolean.opBoolean","INTERSECT",EDGE,{"disambiguationData":[OD(0.0)],"derivedFrom":[makeQuery(id+"F2.opExtrude","SWEPT_FACE",FACE,{"disambiguationData":[OSD([sQuery(id+"F1.wireOp",EDGE,"E11")])]}),makeQuery(id+"F6.opExtrude","SWEPT_FACE",FACE,{"disambiguationData":[OSD([sQuery(id+"F5.wireOp",EDGE,"E28")])]})]});
            var Q7;
            Q7=makeQuery(id+"F6.boolean.opBoolean","INTERSECT",EDGE,{"disambiguationData":[OD(1.0)],"derivedFrom":[makeQuery(id+"F2.opExtrude","SWEPT_FACE",FACE,{"disambiguationData":[OSD([sQuery(id+"F1.wireOp",EDGE,"E11")])]}),makeQuery(id+"F6.opExtrude","SWEPT_FACE",FACE,{"disambiguationData":[OSD([sQuery(id+"F5.wireOp",EDGE,"E27")])]})]});
            var Q8;
            Q8=makeQuery(id+"F6.boolean.opBoolean","INTERSECT",EDGE,{"disambiguationData":[OD(0.0)],"derivedFrom":[makeQuery(id+"F2.opExtrude","SWEPT_FACE",FACE,{"disambiguationData":[OSD([sQuery(id+"F1.wireOp",EDGE,"E11")])]}),makeQuery(id+"F6.opExtrude","SWEPT_FACE",FACE,{"disambiguationData":[OSD([sQuery(id+"F5.wireOp",EDGE,"E27")])]})]});
            var Q9;
            Q9=makeQuery(id+"F6.boolean.opBoolean","INTERSECT",EDGE,{"disambiguationData":[OD(1.0)],"derivedFrom":[makeQuery(id+"F2.opExtrude","SWEPT_FACE",FACE,{"disambiguationData":[OSD([sQuery(id+"F1.wireOp",EDGE,"E11")])]}),makeQuery(id+"F6.opExtrude","SWEPT_FACE",FACE,{"disambiguationData":[OSD([sQuery(id+"F5.wireOp",EDGE,"E26")])]})]});
            var Q10;
            Q10=makeQuery(id+"F6.boolean.opBoolean","INTERSECT",EDGE,{"disambiguationData":[OD(0.0)],"derivedFrom":[makeQuery(id+"F2.opExtrude","SWEPT_FACE",FACE,{"disambiguationData":[OSD([sQuery(id+"F1.wireOp",EDGE,"E11")])]}),makeQuery(id+"F6.opExtrude","SWEPT_FACE",FACE,{"disambiguationData":[OSD([sQuery(id+"F5.wireOp",EDGE,"E26")])]})]});
            var Q11;
            Q11=makeQuery(id+"F6.boolean.opBoolean","INTERSECT",EDGE,{"disambiguationData":[OD(0.0)],"derivedFrom":[makeQuery(id+"F2.opExtrude","SWEPT_FACE",FACE,{"disambiguationData":[OSD([sQuery(id+"F1.wireOp",EDGE,"E11")])]}),makeQuery(id+"F6.opExtrude","SWEPT_FACE",FACE,{"disambiguationData":[OSD([sQuery(id+"F5.wireOp",EDGE,"E25")])]})]});
            fillet(context, id + "F8", {"entities" : qUnion([Q0, Q1, Q2, Q3, Q4, Q5, Q6, Q7, Q8, Q9, Q10, Q11]), "radius" : 5 * mm, "tangentPropagation" : true, "allowEdgeOverflow" : false});
        }
        {
            var Q0;
            {var subQ0=sQuery(id+"F5.wireOp",EDGE,"E31");var subQ1=sQuery(id+"F5.wireOp",EDGE,"E13");var subQ2=makeQuery(id+"F5.imprint","INTERSECT",VERTEX,{"disambiguationData":[OD(0.0)],"derivedFrom":[subQ1,subQ0]});Q0=makeQuery(id+"F5.imprint","IMPRINT",FACE,{"disambiguationData":[TD([[makeQuery(id+"F5.imprint","IMPRINT",EDGE,{"disambiguationData":[TD([[subQ2,-1.0]])],"derivedFrom":subQ1}),-1.0]])]});}
            var Q1;
            {var subQ0=sQuery(id+"F5.wireOp",EDGE,"E31");var subQ1=sQuery(id+"F5.wireOp",EDGE,"E13");var subQ2=makeQuery(id+"F5.imprint","INTERSECT",VERTEX,{"disambiguationData":[OD(0.0)],"derivedFrom":[subQ1,subQ0]});Q1=makeQuery(id+"F5.imprint","IMPRINT",FACE,{"disambiguationData":[TD([[makeQuery(id+"F5.imprint","IMPRINT",EDGE,{"disambiguationData":[TD([[subQ2,-1.0]])],"derivedFrom":subQ1}),1.0]])]});}
            var Q2;
            {var subQ0=sQuery(id+"F5.wireOp",EDGE,"E32");var subQ1=sQuery(id+"F5.wireOp",EDGE,"E13");var subQ2=makeQuery(id+"F5.imprint","INTERSECT",VERTEX,{"disambiguationData":[OD(0.0)],"derivedFrom":[subQ1,subQ0]});Q2=makeQuery(id+"F5.imprint","IMPRINT",FACE,{"disambiguationData":[TD([[makeQuery(id+"F5.imprint","IMPRINT",EDGE,{"disambiguationData":[TD([[subQ2,-1.0]])],"derivedFrom":subQ1}),-1.0]])]});}
            var Q3;
            {var subQ0=sQuery(id+"F5.wireOp",EDGE,"E32");var subQ1=sQuery(id+"F5.wireOp",EDGE,"E13");var subQ2=makeQuery(id+"F5.imprint","INTERSECT",VERTEX,{"disambiguationData":[OD(0.0)],"derivedFrom":[subQ1,subQ0]});Q3=makeQuery(id+"F5.imprint","IMPRINT",FACE,{"disambiguationData":[TD([[makeQuery(id+"F5.imprint","IMPRINT",EDGE,{"disambiguationData":[TD([[subQ2,-1.0]])],"derivedFrom":subQ1}),1.0]])]});}
            var Q4;
            {var subQ0=sQuery(id+"F5.wireOp",EDGE,"E33");var subQ1=sQuery(id+"F5.wireOp",EDGE,"E13");var subQ2=makeQuery(id+"F5.imprint","INTERSECT",VERTEX,{"disambiguationData":[OD(0.0)],"derivedFrom":[subQ1,subQ0]});Q4=makeQuery(id+"F5.imprint","IMPRINT",FACE,{"disambiguationData":[TD([[makeQuery(id+"F5.imprint","IMPRINT",EDGE,{"disambiguationData":[TD([[subQ2,-1.0]])],"derivedFrom":subQ1}),1.0]])]});}
            var Q5;
            {var subQ0=sQuery(id+"F5.wireOp",EDGE,"E33");var subQ1=sQuery(id+"F5.wireOp",EDGE,"E13");var subQ2=makeQuery(id+"F5.imprint","INTERSECT",VERTEX,{"disambiguationData":[OD(0.0)],"derivedFrom":[subQ1,subQ0]});Q5=makeQuery(id+"F5.imprint","IMPRINT",FACE,{"disambiguationData":[TD([[makeQuery(id+"F5.imprint","IMPRINT",EDGE,{"disambiguationData":[TD([[subQ2,-1.0]])],"derivedFrom":subQ1}),-1.0]])]});}
            var Q6;
            {var subQ0=sQuery(id+"F5.wireOp",EDGE,"E34");var subQ1=sQuery(id+"F5.wireOp",EDGE,"E13");var subQ2=makeQuery(id+"F5.imprint","INTERSECT",VERTEX,{"disambiguationData":[OD(0.0)],"derivedFrom":[subQ1,subQ0]});Q6=makeQuery(id+"F5.imprint","IMPRINT",FACE,{"disambiguationData":[TD([[makeQuery(id+"F5.imprint","IMPRINT",EDGE,{"disambiguationData":[TD([[subQ2,-1.0]])],"derivedFrom":subQ1}),1.0]])]});}
            var Q7;
            {var subQ0=sQuery(id+"F5.wireOp",EDGE,"E34");var subQ1=sQuery(id+"F5.wireOp",EDGE,"E13");var subQ2=makeQuery(id+"F5.imprint","INTERSECT",VERTEX,{"disambiguationData":[OD(0.0)],"derivedFrom":[subQ1,subQ0]});Q7=makeQuery(id+"F5.imprint","IMPRINT",FACE,{"disambiguationData":[TD([[makeQuery(id+"F5.imprint","IMPRINT",EDGE,{"disambiguationData":[TD([[subQ2,-1.0]])],"derivedFrom":subQ1}),-1.0]])]});}
            var Q8;
            {var subQ1=sQuery(id+"F5.wireOp",EDGE,"E36.bottom");Q8=makeQuery(id+"F5.imprint","IMPRINT",FACE,{"disambiguationData":[TD([[makeQuery(id+"F5.imprint","IMPRINT",EDGE,{"derivedFrom":subQ1}),-1.0]])]});}
            var Q9;
            {var subQ0=sQuery(id+"F5.wireOp",EDGE,"E36.top");var subQ1=sQuery(id+"F5.wireOp",EDGE,"E13");var subQ2=makeQuery(id+"F5.imprint","INTERSECT",VERTEX,{"derivedFrom":[subQ1,subQ0]});Q9=makeQuery(id+"F5.imprint","IMPRINT",FACE,{"disambiguationData":[TD([[makeQuery(id+"F5.imprint","IMPRINT",EDGE,{"disambiguationData":[TD([[subQ2,-1.0]])],"derivedFrom":subQ1}),1.0]])]});}
            var Q10;
            {var subQ0=sQuery(id+"F5.wireOp",EDGE,"E35");var subQ1=sQuery(id+"F5.wireOp",EDGE,"E13");var subQ2=makeQuery(id+"F5.imprint","INTERSECT",VERTEX,{"disambiguationData":[OD(0.0)],"derivedFrom":[subQ1,subQ0]});Q10=makeQuery(id+"F5.imprint","IMPRINT",FACE,{"disambiguationData":[TD([[makeQuery(id+"F5.imprint","IMPRINT",EDGE,{"disambiguationData":[TD([[subQ2,-1.0]])],"derivedFrom":subQ1}),-1.0]])]});}
            var Q11;
            {var subQ0=sQuery(id+"F5.wireOp",EDGE,"E35");var subQ1=sQuery(id+"F5.wireOp",EDGE,"E13");var subQ2=makeQuery(id+"F5.imprint","INTERSECT",VERTEX,{"disambiguationData":[OD(0.0)],"derivedFrom":[subQ1,subQ0]});Q11=makeQuery(id+"F5.imprint","IMPRINT",FACE,{"disambiguationData":[TD([[makeQuery(id+"F5.imprint","IMPRINT",EDGE,{"disambiguationData":[TD([[subQ2,-1.0]])],"derivedFrom":subQ1}),1.0]])]});}
            extrude(context, id + "F9", {"entities" : qUnion([Q0, Q1, Q2, Q3, Q4, Q5, Q6, Q7, Q8, Q9, Q10, Q11]), "operationType" : NewBodyOperationType.ADD, "depth" : 8 * mm, "offsetDistance" : 25 * mm});
        }
        {
            var Q0;
            Q0=makeQuery(id+"F9.opExtrude","CAP_EDGE",EDGE,{"disambiguationData":[OSD([sQuery(id+"F5.wireOp",EDGE,"E35")])],"isStart":false});
            var Q1;
            Q1=makeQuery(id+"F9.opExtrude","CAP_FACE",FACE,{"disambiguationData":[OSD([sQuery(id+"F5.wireOp",EDGE,"E31")])],"isStart":false});
            var Q2;
            Q2=makeQuery(id+"F9.opExtrude","CAP_FACE",FACE,{"disambiguationData":[OSD([sQuery(id+"F5.wireOp",EDGE,"E32")])],"isStart":false});
            var Q3;
            Q3=makeQuery(id+"F9.opExtrude","CAP_FACE",FACE,{"disambiguationData":[OSD([sQuery(id+"F5.wireOp",EDGE,"E33")])],"isStart":false});
            var Q4;
            Q4=makeQuery(id+"F9.opExtrude","CAP_FACE",FACE,{"disambiguationData":[OSD([sQuery(id+"F5.wireOp",EDGE,"E34")])],"isStart":false});
            var Q5;
            Q5=makeQuery(id+"F9.opExtrude","CAP_EDGE",EDGE,{"disambiguationData":[OSD([sQuery(id+"F5.wireOp",EDGE,"E36.left")])],"isStart":false});
            var Q6;
            Q6=makeQuery(id+"F9.opExtrude","CAP_EDGE",EDGE,{"disambiguationData":[OSD([sQuery(id+"F5.wireOp",EDGE,"E36.right")])],"isStart":false});
            var Q7;
            Q7=makeQuery(id+"F9.opExtrude","CAP_EDGE",EDGE,{"disambiguationData":[OSD([sQuery(id+"F5.wireOp",EDGE,"E36.bottom")])],"isStart":false});
            var Q8;
            Q8=makeQuery(id+"F9.opExtrude","CAP_EDGE",EDGE,{"disambiguationData":[OSD([sQuery(id+"F5.wireOp",EDGE,"E36.top")])],"isStart":false});
            fillet(context, id + "F10", {"entities" : qUnion([Q0, Q1, Q2, Q3, Q4, Q5, Q6, Q7, Q8]), "radius" : .45 * mm, "tangentPropagation" : true, "allowEdgeOverflow" : false});
        }
        {
            var Q0;
            {var subQ0=sQuery(id+"F5.wireOp",EDGE,"E35");var subQ1=sQuery(id+"F5.wireOp",EDGE,"E13");var subQ2=makeQuery(id+"F5.imprint","INTERSECT",VERTEX,{"disambiguationData":[OD(0.0)],"derivedFrom":[subQ1,subQ0]});Q0=makeQuery(id+"F5.imprint","IMPRINT",FACE,{"disambiguationData":[TD([[makeQuery(id+"F5.imprint","IMPRINT",EDGE,{"disambiguationData":[TD([[subQ2,-1.0]])],"derivedFrom":subQ1}),-1.0]])]});}
            var Q1;
            {var subQ0=sQuery(id+"F5.wireOp",EDGE,"E35");var subQ1=sQuery(id+"F5.wireOp",EDGE,"E13");var subQ2=makeQuery(id+"F5.imprint","INTERSECT",VERTEX,{"disambiguationData":[OD(0.0)],"derivedFrom":[subQ1,subQ0]});Q1=makeQuery(id+"F5.imprint","IMPRINT",FACE,{"disambiguationData":[TD([[makeQuery(id+"F5.imprint","IMPRINT",EDGE,{"disambiguationData":[TD([[subQ2,-1.0]])],"derivedFrom":subQ1}),1.0]])]});}
            var Q2;
            {var subQ1=sQuery(id+"F5.wireOp",EDGE,"E36.bottom");Q2=makeQuery(id+"F5.imprint","IMPRINT",FACE,{"disambiguationData":[TD([[makeQuery(id+"F5.imprint","IMPRINT",EDGE,{"derivedFrom":subQ1}),-1.0]])]});}
            var Q3;
            {var subQ0=sQuery(id+"F5.wireOp",EDGE,"E36.top");var subQ1=sQuery(id+"F5.wireOp",EDGE,"E13");var subQ2=makeQuery(id+"F5.imprint","INTERSECT",VERTEX,{"derivedFrom":[subQ1,subQ0]});Q3=makeQuery(id+"F5.imprint","IMPRINT",FACE,{"disambiguationData":[TD([[makeQuery(id+"F5.imprint","IMPRINT",EDGE,{"disambiguationData":[TD([[subQ2,-1.0]])],"derivedFrom":subQ1}),1.0]])]});}
            var Q4;
            {var subQ0=sQuery(id+"F5.wireOp",EDGE,"E34");var subQ1=sQuery(id+"F5.wireOp",EDGE,"E13");var subQ2=makeQuery(id+"F5.imprint","INTERSECT",VERTEX,{"disambiguationData":[OD(0.0)],"derivedFrom":[subQ1,subQ0]});Q4=makeQuery(id+"F5.imprint","IMPRINT",FACE,{"disambiguationData":[TD([[makeQuery(id+"F5.imprint","IMPRINT",EDGE,{"disambiguationData":[TD([[subQ2,-1.0]])],"derivedFrom":subQ1}),1.0]])]});}
            var Q5;
            {var subQ0=sQuery(id+"F5.wireOp",EDGE,"E34");var subQ1=sQuery(id+"F5.wireOp",EDGE,"E13");var subQ2=makeQuery(id+"F5.imprint","INTERSECT",VERTEX,{"disambiguationData":[OD(0.0)],"derivedFrom":[subQ1,subQ0]});Q5=makeQuery(id+"F5.imprint","IMPRINT",FACE,{"disambiguationData":[TD([[makeQuery(id+"F5.imprint","IMPRINT",EDGE,{"disambiguationData":[TD([[subQ2,-1.0]])],"derivedFrom":subQ1}),-1.0]])]});}
            var Q6;
            {var subQ0=sQuery(id+"F5.wireOp",EDGE,"E33");var subQ1=sQuery(id+"F5.wireOp",EDGE,"E13");var subQ2=makeQuery(id+"F5.imprint","INTERSECT",VERTEX,{"disambiguationData":[OD(0.0)],"derivedFrom":[subQ1,subQ0]});Q6=makeQuery(id+"F5.imprint","IMPRINT",FACE,{"disambiguationData":[TD([[makeQuery(id+"F5.imprint","IMPRINT",EDGE,{"disambiguationData":[TD([[subQ2,-1.0]])],"derivedFrom":subQ1}),1.0]])]});}
            var Q7;
            {var subQ0=sQuery(id+"F5.wireOp",EDGE,"E33");var subQ1=sQuery(id+"F5.wireOp",EDGE,"E13");var subQ2=makeQuery(id+"F5.imprint","INTERSECT",VERTEX,{"disambiguationData":[OD(0.0)],"derivedFrom":[subQ1,subQ0]});Q7=makeQuery(id+"F5.imprint","IMPRINT",FACE,{"disambiguationData":[TD([[makeQuery(id+"F5.imprint","IMPRINT",EDGE,{"disambiguationData":[TD([[subQ2,-1.0]])],"derivedFrom":subQ1}),-1.0]])]});}
            var Q8;
            {var subQ0=sQuery(id+"F5.wireOp",EDGE,"E32");var subQ1=sQuery(id+"F5.wireOp",EDGE,"E13");var subQ2=makeQuery(id+"F5.imprint","INTERSECT",VERTEX,{"disambiguationData":[OD(0.0)],"derivedFrom":[subQ1,subQ0]});Q8=makeQuery(id+"F5.imprint","IMPRINT",FACE,{"disambiguationData":[TD([[makeQuery(id+"F5.imprint","IMPRINT",EDGE,{"disambiguationData":[TD([[subQ2,-1.0]])],"derivedFrom":subQ1}),1.0]])]});}
            var Q9;
            {var subQ0=sQuery(id+"F5.wireOp",EDGE,"E32");var subQ1=sQuery(id+"F5.wireOp",EDGE,"E13");var subQ2=makeQuery(id+"F5.imprint","INTERSECT",VERTEX,{"disambiguationData":[OD(0.0)],"derivedFrom":[subQ1,subQ0]});Q9=makeQuery(id+"F5.imprint","IMPRINT",FACE,{"disambiguationData":[TD([[makeQuery(id+"F5.imprint","IMPRINT",EDGE,{"disambiguationData":[TD([[subQ2,-1.0]])],"derivedFrom":subQ1}),-1.0]])]});}
            var Q10;
            {var subQ0=sQuery(id+"F5.wireOp",EDGE,"E31");var subQ1=sQuery(id+"F5.wireOp",EDGE,"E13");var subQ2=makeQuery(id+"F5.imprint","INTERSECT",VERTEX,{"disambiguationData":[OD(0.0)],"derivedFrom":[subQ1,subQ0]});Q10=makeQuery(id+"F5.imprint","IMPRINT",FACE,{"disambiguationData":[TD([[makeQuery(id+"F5.imprint","IMPRINT",EDGE,{"disambiguationData":[TD([[subQ2,-1.0]])],"derivedFrom":subQ1}),-1.0]])]});}
            var Q11;
            {var subQ0=sQuery(id+"F5.wireOp",EDGE,"E31");var subQ1=sQuery(id+"F5.wireOp",EDGE,"E13");var subQ2=makeQuery(id+"F5.imprint","INTERSECT",VERTEX,{"disambiguationData":[OD(0.0)],"derivedFrom":[subQ1,subQ0]});Q11=makeQuery(id+"F5.imprint","IMPRINT",FACE,{"disambiguationData":[TD([[makeQuery(id+"F5.imprint","IMPRINT",EDGE,{"disambiguationData":[TD([[subQ2,-1.0]])],"derivedFrom":subQ1}),1.0]])]});}
            extrude(context, id + "F11", {"entities" : qUnion([Q0, Q1, Q2, Q3, Q4, Q5, Q6, Q7, Q8, Q9, Q10, Q11]), "operationType" : NewBodyOperationType.REMOVE, "depth" : 1.8 * mm, "offsetDistance" : 25 * mm});
        }
        {
            var Q0;
            Q0=qCreatedBy(makeId("Top.planeOp"),FACE);
            var sketch = newSketch(context, id + "F12", { "sketchPlane" : qUnion([Q0])});
            skCircle(sketch, "E37", {"center": v(0, 0) * mm, "radius": 13.47 * mm});
            skSolve(sketch);
        }
        {
            var Q0;
            Q0 = qSketchRegion(id + "F12", true);
            extrude(context, id + "F13", {"entities" : qUnion([Q0]), "operationType" : NewBodyOperationType.REMOVE, "depth" : 1 * mm, "offsetDistance" : 25 * mm});
        }
        {
            var Q0;
            {var subQ0=sQuery(id+"F0.wireOp",EDGE,"E9.right");var subQ1=sQuery(id+"F0.wireOp",EDGE,"E1.0");var subQ2=makeQuery(id+"F0.imprint","INTERSECT",VERTEX,{"disambiguationData":[OD(1.0)],"derivedFrom":[subQ1,subQ0]});Q0=makeQuery(id+"F0.imprint","IMPRINT",FACE,{"disambiguationData":[TD([[makeQuery(id+"F0.imprint","IMPRINT",EDGE,{"disambiguationData":[TD([[subQ2,-1.0]])],"derivedFrom":subQ1}),1.0]])]});}
            var Q1;
            {var subQ0=sQuery(id+"F0.wireOp",EDGE,"E3.right");var subQ1=sQuery(id+"F0.wireOp",EDGE,"E1.0");var subQ2=makeQuery(id+"F0.imprint","INTERSECT",VERTEX,{"disambiguationData":[OD(0.0)],"derivedFrom":[subQ1,subQ0]});Q1=makeQuery(id+"F0.imprint","IMPRINT",FACE,{"disambiguationData":[TD([[makeQuery(id+"F0.imprint","IMPRINT",EDGE,{"disambiguationData":[TD([[subQ2,1.0]])],"derivedFrom":subQ1}),1.0]])]});}
            var Q2;
            {var subQ0=sQuery(id+"F0.wireOp",EDGE,"E3.left");var subQ1=sQuery(id+"F0.wireOp",EDGE,"E1.0");var subQ2=makeQuery(id+"F0.imprint","INTERSECT",VERTEX,{"disambiguationData":[OD(0.0)],"derivedFrom":[subQ1,subQ0]});Q2=makeQuery(id+"F0.imprint","IMPRINT",FACE,{"disambiguationData":[TD([[makeQuery(id+"F0.imprint","IMPRINT",EDGE,{"disambiguationData":[TD([[subQ2,-1.0]])],"derivedFrom":subQ1}),1.0]])]});}
            var Q3;
            {var subQ0=sQuery(id+"F0.wireOp",EDGE,"E3.right");var subQ1=sQuery(id+"F0.wireOp",EDGE,"E1.0");var subQ2=makeQuery(id+"F0.imprint","INTERSECT",VERTEX,{"disambiguationData":[OD(1.0)],"derivedFrom":[subQ1,subQ0]});Q3=makeQuery(id+"F0.imprint","IMPRINT",FACE,{"disambiguationData":[TD([[makeQuery(id+"F0.imprint","IMPRINT",EDGE,{"disambiguationData":[TD([[subQ2,-1.0]])],"derivedFrom":subQ1}),1.0]])]});}
            var Q4;
            {var subQ0=sQuery(id+"F0.wireOp",EDGE,"E2.right");var subQ1=sQuery(id+"F0.wireOp",EDGE,"E1.0");var subQ2=makeQuery(id+"F0.imprint","INTERSECT",VERTEX,{"disambiguationData":[OD(1.0)],"derivedFrom":[subQ1,subQ0]});Q4=makeQuery(id+"F0.imprint","IMPRINT",FACE,{"disambiguationData":[TD([[makeQuery(id+"F0.imprint","IMPRINT",EDGE,{"disambiguationData":[TD([[subQ2,-1.0]])],"derivedFrom":subQ1}),1.0]])]});}
            extrude(context, id + "F14", {"entities" : qUnion([Q0, Q1, Q2, Q3, Q4]), "operationType" : NewBodyOperationType.REMOVE, "depth" : 1 * mm, "offsetDistance" : 25 * mm});
        }
        {
            var Q0;
            Q0=makeQuery(id+"F14.boolean.opBoolean","COPY",EDGE,{"derivedFrom":makeQuery(id+"F14.opExtrude","SWEPT_EDGE",EDGE,{"disambiguationData":[OSD([sQuery(id+"F0.wireOp",EDGE,"E1.0"),sQuery(id+"F0.wireOp",EDGE,"E8.left")])]})});
            var Q1;
            Q1=makeQuery(id+"F14.boolean.opBoolean","COPY",EDGE,{"derivedFrom":makeQuery(id+"F14.opExtrude","SWEPT_EDGE",EDGE,{"disambiguationData":[OSD([sQuery(id+"F0.wireOp",EDGE,"E1.0"),sQuery(id+"F0.wireOp",EDGE,"E9.right")])]})});
            var Q2;
            Q2=makeQuery(id+"F14.boolean.opBoolean","COPY",EDGE,{"derivedFrom":makeQuery(id+"F14.opExtrude","SWEPT_EDGE",EDGE,{"disambiguationData":[OSD([sQuery(id+"F0.wireOp",EDGE,"E1.0"),sQuery(id+"F0.wireOp",EDGE,"E2.left")])]})});
            var Q3;
            {var subQ0=sQuery(id+"F0.wireOp",EDGE,"E2.right");var subQ1=sQuery(id+"F0.wireOp",EDGE,"E1.0");Q3=makeQuery(id+"F14.boolean.opBoolean","COPY",EDGE,{"derivedFrom":makeQuery(id+"F14.opExtrude","SWEPT_EDGE",EDGE,{"disambiguationData":[OSD([subQ1,subQ0]),TDD([makeQuery(id+"F0.imprint","INTERSECT",VERTEX,{"disambiguationData":[OD(1.0)],"derivedFrom":[subQ1,subQ0]})])]})});}
            var Q4;
            {var subQ0=sQuery(id+"F0.wireOp",EDGE,"E3.right");var subQ1=sQuery(id+"F0.wireOp",EDGE,"E1.0");Q4=makeQuery(id+"F14.boolean.opBoolean","COPY",EDGE,{"derivedFrom":makeQuery(id+"F14.opExtrude","SWEPT_EDGE",EDGE,{"disambiguationData":[OSD([subQ1,subQ0]),TDD([makeQuery(id+"F0.imprint","INTERSECT",VERTEX,{"disambiguationData":[OD(1.0)],"derivedFrom":[subQ1,subQ0]})])]})});}
            var Q5;
            Q5=makeQuery(id+"F14.boolean.opBoolean","COPY",EDGE,{"derivedFrom":makeQuery(id+"F14.opExtrude","SWEPT_EDGE",EDGE,{"disambiguationData":[OSD([sQuery(id+"F0.wireOp",EDGE,"E1.0"),sQuery(id+"F0.wireOp",EDGE,"E7.top")])]})});
            var Q6;
            Q6=makeQuery(id+"F14.boolean.opBoolean","COPY",EDGE,{"derivedFrom":makeQuery(id+"F14.opExtrude","SWEPT_EDGE",EDGE,{"disambiguationData":[OSD([sQuery(id+"F0.wireOp",EDGE,"E1.0"),sQuery(id+"F0.wireOp",EDGE,"E3.left")])]})});
            var Q7;
            Q7=makeQuery(id+"F14.boolean.opBoolean","COPY",EDGE,{"derivedFrom":makeQuery(id+"F14.opExtrude","SWEPT_EDGE",EDGE,{"disambiguationData":[OSD([sQuery(id+"F0.wireOp",EDGE,"E1.0"),sQuery(id+"F0.wireOp",EDGE,"E6.bottom")])]})});
            var Q8;
            {var subQ0=sQuery(id+"F0.wireOp",EDGE,"E2.right");var subQ1=sQuery(id+"F0.wireOp",EDGE,"E1.0");Q8=makeQuery(id+"F14.boolean.opBoolean","COPY",EDGE,{"derivedFrom":makeQuery(id+"F14.opExtrude","SWEPT_EDGE",EDGE,{"disambiguationData":[OSD([subQ1,subQ0]),TDD([makeQuery(id+"F0.imprint","INTERSECT",VERTEX,{"disambiguationData":[OD(0.0)],"derivedFrom":[subQ1,subQ0]})])]})});}
            var Q9;
            {var subQ0=sQuery(id+"F0.wireOp",EDGE,"E3.right");var subQ1=sQuery(id+"F0.wireOp",EDGE,"E1.0");Q9=makeQuery(id+"F14.boolean.opBoolean","COPY",EDGE,{"derivedFrom":makeQuery(id+"F14.opExtrude","SWEPT_EDGE",EDGE,{"disambiguationData":[OSD([subQ1,subQ0]),TDD([makeQuery(id+"F0.imprint","INTERSECT",VERTEX,{"disambiguationData":[OD(0.0)],"derivedFrom":[subQ1,subQ0]})])]})});}
            fillet(context, id + "F15", {"entities" : qUnion([Q0, Q1, Q2, Q3, Q4, Q5, Q6, Q7, Q8, Q9]), "radius" : 1 * mm, "tangentPropagation" : true, "allowEdgeOverflow" : false});
        }
    });
